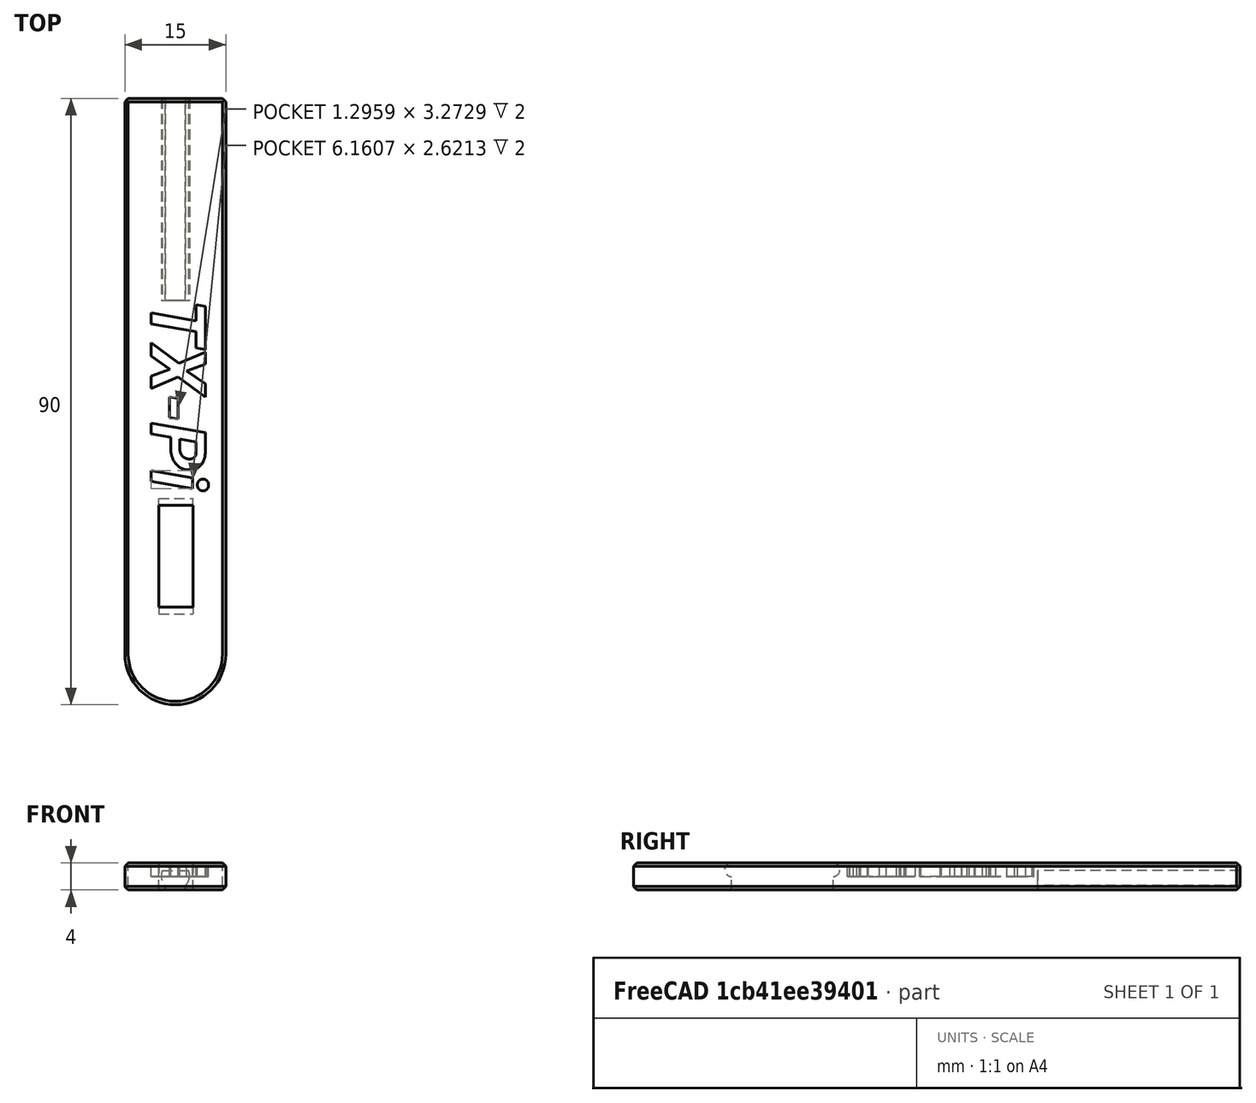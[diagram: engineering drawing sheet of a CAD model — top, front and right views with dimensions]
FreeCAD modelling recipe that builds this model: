
FCSTD DOCUMENT  (FreeCAD 0.17RUnknown)
Label: TX-Pi_stand_support_right
License: All rights reserved
LicenseURL: http://en.wikipedia.org/wiki/All_rights_reserved
objects: Part::Cut×6, Part::Box×4, Part::Cylinder×4, Part::Chamfer×3, Part::MultiFuse×2, Part::Part2DObjectPython×1, Part::Extrusion×1
note: 21 computed .brp shape members not serialized (recipe doc carries the construction recipe); baked Part::Feature solids carry a one-line shape summary decoded from their .brp

FEATURE [Part::Box] Box  label="Würfel"
  AttacherType = Attacher::AttachEngine3D
  Height = 4
  Length = 15
  Width = 82.5
FEATURE [Part::Cylinder] Cylinder  label="Zylinder"
  Angle = 360
  AttacherType = Attacher::AttachEngine3D
  Height = 4
  Placement = pos=(7.5,0,0) rot=(0,0,1;0rad)
  Radius = 7.5
FEATURE [Part::MultiFuse] Fusion
  Shapes = -> [Box,Cylinder]
FEATURE [Part::Chamfer] Chamfer
  Base = -> Fusion
  Edges = 4 edges r=0.5: [Edge3,Edge9,Edge11,Edge15]
FEATURE [Part::Chamfer] Chamfer001
  Base = -> Chamfer
  Edges = 4 edges r=0.5: [Edge3,Edge7,Edge13,Edge18]
FEATURE [Part::Chamfer] Chamfer002
  Base = -> Chamfer001
  Edges = 2 edges r=0.5: [Edge1,Edge4]
FEATURE [Part::Cylinder] Cylinder001  label="Zylinder001"
  Angle = 360
  AttacherType = Attacher::AttachEngine3D
  Height = 30
  Placement = pos=(7.5,82.5,2.1) rot=(1,0,0;1.5708rad)
  Radius = 2.1
FEATURE [Part::Box] Box001  label="Würfel001"
  AttacherType = Attacher::AttachEngine3D
  Height = 3
  Length = 4
  Placement = pos=(5.5,52.5,2.9) rot=(0,0,1;0rad)
  Width = 30
FEATURE [Part::Box] Box002  label="Würfel002"
  AttacherType = Attacher::AttachEngine3D
  Height = 3
  Length = 3
  Placement = pos=(6,52.5,-1) rot=(0,0,1;0rad)
  Width = 30
FEATURE [Part::MultiFuse] Fusion001
  Shapes = -> [Cylinder001,Box002]
FEATURE [Part::Cut] Cut
  Base = -> Fusion001
  Tool = -> Box001
FEATURE [Part::Cut] Cut001
  Base = -> Chamfer002
  Tool = -> Cut
FEATURE [Part::Box] Box003  label="Würfel003"
  AttacherType = Attacher::AttachEngine3D
  Height = 5
  Length = 5.1
  Placement = pos=(5.05,7,-0.5) rot=(0,0,1;0rad)
  Width = 15.1
FEATURE [Part::Cut] Cut002
  Base = -> Cut001
  Tool = -> Box003
FEATURE [Part::Cylinder] Cylinder002  label="Zylinder002"
  Angle = 360
  AttacherType = Attacher::AttachEngine3D
  Height = 5.1
  Placement = pos=(5.05,22.1,3) rot=(0,1,0;1.5708rad)
  Radius = 1
FEATURE [Part::Cylinder] Cylinder003  label="Zylinder003"
  Angle = 360
  AttacherType = Attacher::AttachEngine3D
  Height = 5.1
  Placement = pos=(5.05,7,3) rot=(0,1,0;1.5708rad)
  Radius = 1
FEATURE [Part::Cut] Cut003
  Base = -> Cut002
  Tool = -> Cylinder002
FEATURE [Part::Cut] Cut004
  Base = -> Cut003
  Tool = -> Cylinder003
FEATURE [Part::Part2DObjectPython] ShapeString  # Draft 2D object (typed FeaturePython)
  FontFile = <path>
  Placement = pos=(-9.1754,-3.35448,0) rot=(0,0,1;0rad)
  Size = 10
  String = TX-Pi
  Tracking = 0
FEATURE [Part::Extrusion] Extrude
  Base = -> ShapeString
  Dir = (0,0,7)
  DirMode = 0
  FaceMakerClass = Part::FaceMakerExtrusion
  LengthFwd = 0
  LengthRev = 0
  Placement = pos=(7.25,43.5,2) rot=(0,0,-1;1.5708rad)
  Solid = true
  Symmetric = false
FEATURE [Part::Cut] Cut005
  Base = -> Cut004
  Tool = -> Extrude
note: 1 file-system path scrubbed to <path> (originals preserved in the JSON sidecar)
